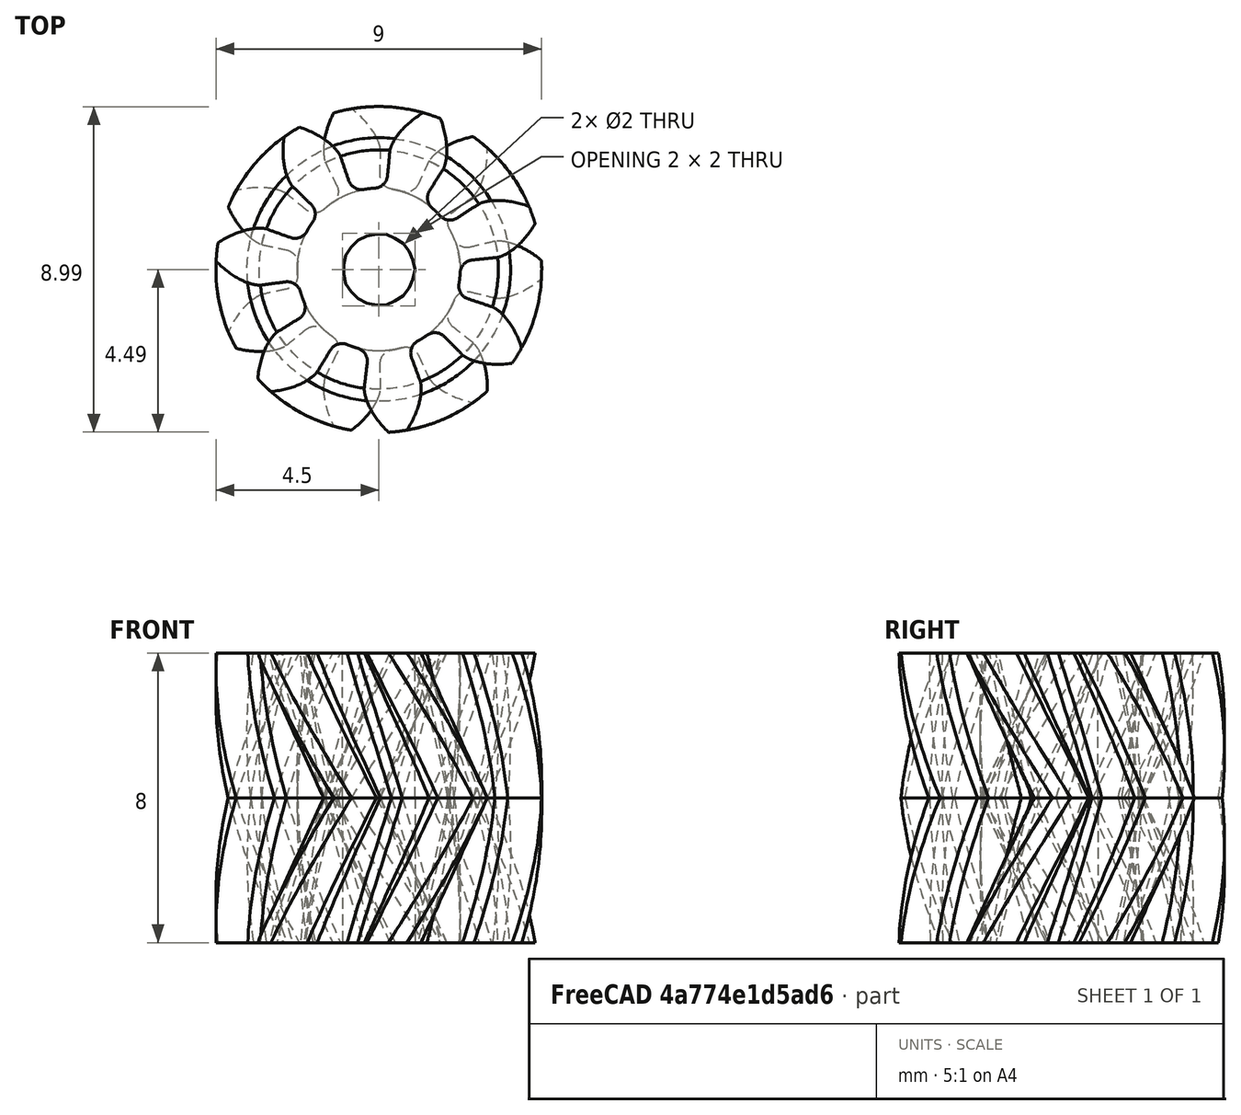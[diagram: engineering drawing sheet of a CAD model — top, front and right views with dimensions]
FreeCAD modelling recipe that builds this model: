
FCSTD DOCUMENT  (FreeCAD 0.17R13541 (Git))
Label: Gear5d
License: All rights reserved
LicenseURL: http://en.wikipedia.org/wiki/All_rights_reserved
objects: Part::Helix×2, Part::Sweep×2, Part::Cylinder×2, Part::Cut×2, Part::Part2DObjectPython×1, Part::Fuse×1
note: 10 computed .brp shape members not serialized (recipe doc carries the construction recipe); baked Part::Feature solids carry a one-line shape summary decoded from their .brp

FEATURE [Part::Part2DObjectPython] InvoluteGear  # Draft 2D object (typed FeaturePython)
  ExternalGear = true
  HighPrecision = true
  Modules = 1
  NumberOfTeeth = 7
  PressureAngle = 20
FEATURE [Part::Helix] Helix002
  Angle = 0
  AttacherType = Attacher::AttachEngine3D
  Height = 4
  LocalCoord = 1
  Pitch = 45.16
  Radius = 4.5
  Style = 1
FEATURE [Part::Sweep] Sweep
  Frenet = true
  Sections = -> [InvoluteGear]
  Solid = true
  Spine = -> Helix002 [Edge1]
  Transition = 1
FEATURE [Part::Helix] Helix
  Angle = 0
  AttacherType = Attacher::AttachEngine3D
  Height = 4
  LocalCoord = 0
  Pitch = 45.16
  Placement = pos=(0,0,0) rot=(1,0,0;3.14159rad)
  Radius = 4.5
  Style = 1
FEATURE [Part::Sweep] Sweep001
  Frenet = true
  Sections = -> [InvoluteGear]
  Solid = true
  Spine = -> Helix [Edge1]
  Transition = 1
FEATURE [Part::Cylinder] Cylinder
  Angle = 360
  AttacherType = Attacher::AttachEngine3D
  Height = 4.01
  Radius = 1
FEATURE [Part::Cylinder] Cylinder001
  Angle = 360
  AttacherType = Attacher::AttachEngine3D
  Height = 4.01
  Placement = pos=(0,0,0) rot=(1,0,0;3.14159rad)
  Radius = 1
FEATURE [Part::Cut] Cut
  Base = -> Sweep
  Tool = -> Cylinder
FEATURE [Part::Cut] Cut001
  Base = -> Sweep001
  Tool = -> Cylinder001
FEATURE [Part::Fuse] Fusion
  Base = -> Cut
  Tool = -> Cut001
